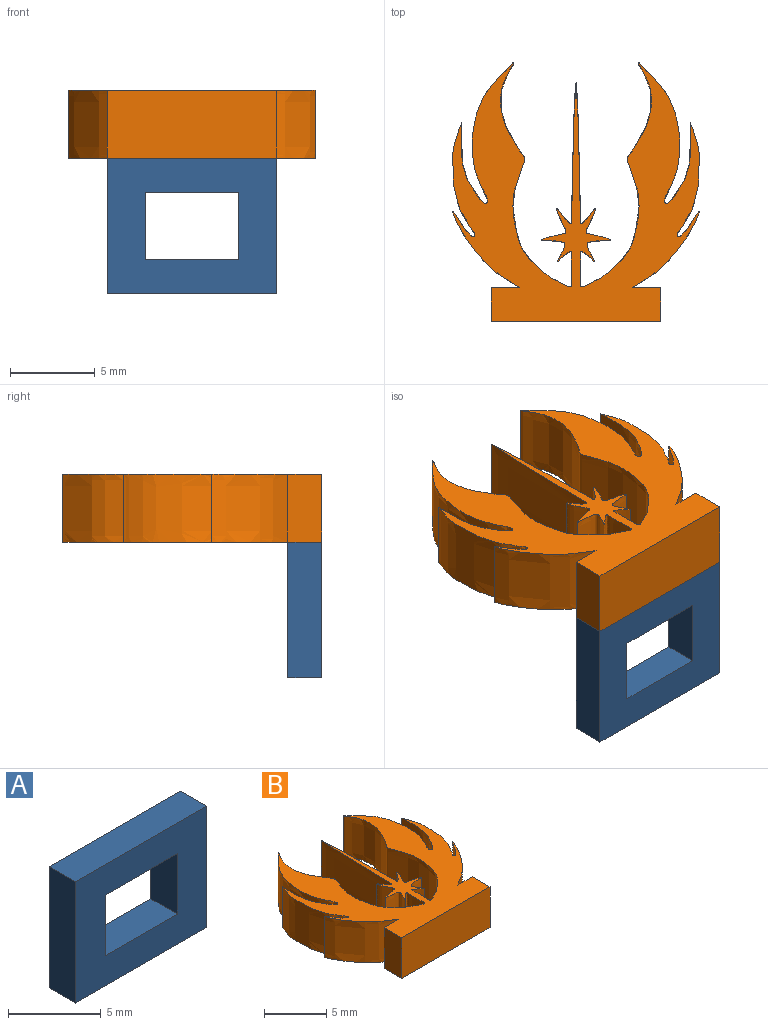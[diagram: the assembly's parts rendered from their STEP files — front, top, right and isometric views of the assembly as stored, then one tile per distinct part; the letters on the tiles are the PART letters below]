
ASSEMBLY  parts=2 mates=3
PART A: 10 faces, bbox 10x2x8 mm
  f0: plane 10x8mm, normal (0,-1,0), area 58mm2, adj f1,f3,f4,f5,f6,f7,f8,f9
  f1: plane 8x2mm, normal (1,0,0), area 16mm2, adj f0,f2,f4,f5
  f2: plane 10x8mm, normal (0,1,0), area 58mm2, adj f1,f3,f4,f5,f6,f7,f8,f9
  f3: plane 8x2mm, normal (-1,0,0), area 16mm2, adj f0,f2,f4,f5
  f4: plane 10x2mm, normal (0,0,-1), area 20mm2, adj f0,f1,f2,f3
  f5: plane 10x2mm, normal (0,0,1), area 20mm2, adj f0,f1,f2,f3
  f6: plane 5.5x2mm, normal (0,0,-1), area 11mm2, adj f0,f2,f7,f9
  f7: plane 4x2mm, normal (1,0,0), area 8mm2, adj f0,f2,f6,f8
  f8: plane 5.5x2mm, normal (0,0,1), area 11mm2, adj f0,f2,f7,f9
  f9: plane 4x2mm, normal (-1,0,0), area 8mm2, adj f0,f2,f6,f8
PART B: 9 faces, bbox 14.7x15.4x4 mm
  f0: extruded ~13.23x7.25mm, area 276.7mm2, adj f1,f6,f7,f8
  f1: plane 4x1.67mm, normal (0,1,0), area 6.7mm2, adj f0,f2,f7,f8
  f2: plane 4x2mm, normal (-1,0,0), area 8mm2, adj f1,f3,f7,f8
  f3: plane 10x4mm, normal (0,-1,0), area 40mm2, adj f2,f4,f7,f8
  f4: plane 4x2mm, normal (1,0,0), area 8mm2, adj f3,f5,f7,f8
  f5: plane 4x1.67mm, normal (0,1,0), area 6.7mm2, adj f4,f6,f7,f8
  f6: extruded ~13.23x7.25mm, area 276.7mm2, adj f0,f5,f7,f8
  f7: plane 15.39x14.65mm, normal (0,0,1), area 85.5mm2, adj f0,f1,f2,f3,f4,f5,f6
  f8: plane 15.39x14.65mm, normal (0,0,-1), area 85.5mm2, adj f0,f1,f2,f3,f4,f5,f6
PLACE A t=(-1.2,-2.14,11.24)mm
PLACE B t=(-1.2,-1.87,11.24)mm
MATE parallel A.f3 <-> B.f2  axis (-1,0,0) through (-6.2,-2.14,7.24)mm
MATE parallel A.f0 <-> B.f3  axis (0,-1,0) through (3.8,-3.14,7.24)mm
MATE planar A.f5 <-> B.f8  axis (0,0,1) through (-1.2,-2.14,11.24)mm
